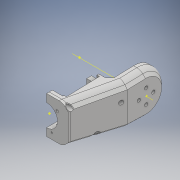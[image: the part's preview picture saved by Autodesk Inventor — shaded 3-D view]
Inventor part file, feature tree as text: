
AUTODESK INVENTOR PART (.ipt)
format: ipt  version: 2018 (Build 220112000, 112)  size: 1,074,688 bytes
history: native  units: mm
features: projected_geometry x48, sketch x45, extrude x37, hole x13, fillet x11, other x10, chamfer x9, reference x3, mirror x1, plane x1
ambient origin geometry x8: Origin, YZ Plane, XZ Plane, XY Plane, X Axis, Y Axis, Z Axis, Center Point
bodies: Solid1 (feature_tree)
feature tree (178):
  extrude  "Extrusion1"  Depth=45.0mm
  extrude  "Extrusion2"  Depth=2.25mm
  hole  "Hole1"  [1 undecoded]
  hole  "Hole2"  [1 undecoded]
  fillet  "Fillet1"  Radius=14.0mm
  extrude  "Extrusion3"  Depth=18.5mm
  extrude  "Extrusion4"  Depth=10.0mm
  extrude  "Extrusion5"  Depth=2.0mm
  extrude  "Extrusion6"  Depth=2.0mm
  hole  "Hole3"  [1 undecoded]
  extrude  "Extrusion7"  Depth=2.0mm
  extrude  "Extrusion8"  Depth=1.0mm TaperAngle=0.0deg
  extrude  "Extrusion9"  Depth=24.5mm
  extrude  "Extrusion10"  Depth=10.0mm
  extrude  "Extrusion11"  Depth=14.5mm
  extrude  "Extrusion13"  Depth=14.5mm
  extrude  "Extrusion14"  Depth=5.0mm
  extrude  "Extrusion15"  Depth=2.25mm
  extrude  "Extrusion16"  Depth=5.0mm
  extrude  "Extrusion17"  Depth=9.0mm
  chamfer  "Chamfer1"  Distance=1.0mm
  fillet  "Fillet7"  Radius=20.7mm
  fillet  "Fillet8"  Radius=32.0mm
  mirror  "Mirror1"
  sketch  "Sketch26"  dims[d55=2.25mm d56=5.0mm]
  extrude  "Extrusion24"  Depth=1.0mm TaperAngle=0.0deg
  extrude  "Extrusion25"  Depth=8.0mm
  extrude  "Extrusion26"  Depth=0.2mm TaperAngle=0.0deg
  extrude  "Extrusion27"  Depth=5.0mm TaperAngle=0.0deg
  other  "Work Axis1"
  plane  "Work Plane2"
  extrude  "Extrusion28"  Depth=0.2mm TaperAngle=0.0deg
  extrude  "Extrusion29"  Depth=2.0mm TaperAngle=45.0deg
  chamfer  "Chamfer2"  Distance=15.0mm
  extrude  "Extrusion31"  Depth=15.0mm TaperAngle=0.0deg
  chamfer  "Chamfer3"  Distance=15.0mm
  chamfer  "Chamfer4"  Distance=100.0mm
  extrude  "Extrusion32"  Depth=2.0mm TaperAngle=45.0deg
  chamfer  "Chamfer5"  [1 undecoded]
  extrude  "Extrusion33"  Depth=2.0mm
  sketch  "Sketch41"  dims[d100=0.2mm d101=0.0mm d102=2.5mm d103=2.0mm d104=45.0deg]
  extrude  "Extrusion34"  Depth=2.0mm
  chamfer  "Chamfer6"  Distance=11.5mm
  fillet  "Fillet9"  Radius=100.0mm
  extrude  "Extrusion35"  Depth=2.0mm TaperAngle=45.0deg
  extrude  "Extrusion36"  Depth=2.0mm TaperAngle=45.0deg
  chamfer  "Chamfer7"  Distance=7.0mm
  fillet  "Fillet10"  Radius=100.0mm
  extrude  "Extrusion37"  Depth=2.0mm TaperAngle=45.0deg
  extrude  "Extrusion38"  Depth=2.0mm TaperAngle=0.0deg
  extrude  "Extrusion39"  Depth=2.0mm TaperAngle=0.0deg
  extrude  "Extrusion40"  Depth=2.0mm TaperAngle=45.0deg
  chamfer  "Chamfer8"  Distance=8.0mm
  chamfer  "Chamfer9"  Angle=15.0deg  [1 undecoded]
  hole  "Hole6"  [1 undecoded]
  fillet  "Fillet11"  Radius=15.470628mm
  fillet  "Fillet12"  Radius=2.5mm
  extrude  "Extrusion41"  Depth=2.0mm TaperAngle=0.0deg
  extrude  "Extrusion42"  Depth=2.0mm TaperAngle=45.0deg
  hole  "Hole7"  [1 undecoded]
  extrude  "Extrusion43"  TaperAngle=15.0deg  [1 undecoded]
  extrude  "Extrusion44"  Depth=2.0mm
  sketch  "Sketch58"  dims[d162=5.0mm d165=100.0mm d166=0.0mm]
  hole  "Hole8"  [1 undecoded]
  hole  "Hole9"  [1 undecoded]
  hole  "Hole10"  [1 undecoded]
  hole  "Hole11"  [1 undecoded]
  hole  "Hole12"  [1 undecoded]
  hole  "Hole13"  [1 undecoded]
  hole  "Hole14"  [1 undecoded]
  hole  "Hole15"  [1 undecoded]
  extrude  "Extrusion45"  Depth=2.0mm
  fillet  "Fillet14"  Radius=0.75mm
  fillet  "Fillet15"  Radius=20.5mm
  fillet  "Fillet16"  Radius=3.05mm
  fillet  "Fillet17"  Radius=14.0mm
  sketch  "Sketch1"  dims[d0=24.5mm d1=45.0mm]
  sketch  "Sketch2"  dims[d2=1.95mm d3=0.0mm d4=2.25mm]
  projected_geometry  "Projected Loop1"
  sketch  "Sketch3"  dims[d5=20.0mm d6=2.25mm]
  projected_geometry  "Projected Loop2"
  sketch  "Sketch4"  dims[d7=5.25mm d8=5.25mm d9=14.0mm]
  projected_geometry  "Projected Loop3"
  sketch  "Sketch5"  dims[d10=5.25mm d11=18.5mm]
  projected_geometry  "Projected Loop4"
  sketch  "Sketch6"  dims[d12=10.0mm d13=0.0mm d14=20.5mm]
  projected_geometry  "Projected Loop5"
  sketch  "Sketch7"  dims[d15=2.0mm d16=2.195mm]
  projected_geometry  "Projected Loop6"
  sketch  "Sketch8"  dims[d17=2.0mm]
  projected_geometry  "Projected Loop7"
  sketch  "Sketch9"  dims[d18=2.4mm d19=6.0mm d20=4.4mm d21=2.0mm d22=90.0deg d23=8.0mm d24=20.594885mm d25=20.5mm]
  projected_geometry  "Projected Loop8"
  projected_geometry  "Projected Loop9"
  sketch  "Sketch10"  dims[d26=26.65mm d27=2.0mm]
  projected_geometry  "Projected Loop10"
  projected_geometry  "Projected Loop11"
  sketch  "Sketch11"  dims[d28=2.0mm]
  projected_geometry  "Projected Loop12"
  sketch  "Sketch12"  dims[d29=2.4mm d30=6.0mm d31=4.4mm d32=2.0mm d33=90.0deg d34=8.0mm d35=20.594885mm d36=0.5mm]
  sketch  "Sketch13"  dims[d37=18.0mm d38=1.0mm d39=0.0mm]
  sketch  "Sketch14"  dims[d41=5.0mm d42=0.0mm d43=24.5mm]
  projected_geometry  "Projected Loop13"
  sketch  "Sketch16"  dims[d44=1.15mm d45=0.0mm d46=10.0mm]
  projected_geometry  "Projected Loop14"
  sketch  "Sketch17"  dims[d47=21.0mm d48=14.5mm]
  projected_geometry  "Projected Loop15"
  sketch  "Sketch18"  dims[d49=20.0mm d50=14.5mm]
  projected_geometry  "Projected Loop16"
  sketch  "Sketch19"  dims[d51=24.5mm d52=5.0mm]
  projected_geometry  "Projected Loop17"
  sketch  "Sketch20"  dims[d53=5.0mm d54=2.25mm]
  projected_geometry  "Projected Loop18"
  projected_geometry  "Projected Loop25"
  sketch  "Sketch31"  dims[d57=5.0mm d58=9.0mm]
  projected_geometry  "Projected Loop30"
  reference  "Reference1"
  sketch  "Sketch32"  dims[d59=14.75mm]
  projected_geometry  "Projected Loop31"
  sketch  "Sketch33"  dims[d60=4.0mm d61=1.0mm d62=0.0mm d63=20.7mm]
  projected_geometry  "Projected Loop32"
  sketch  "Sketch34"  dims[d64=2.4mm d65=6.0mm d66=4.4mm d67=2.0mm d68=90.0deg d69=8.0mm d70=20.594885mm d72=32.0mm]
  projected_geometry  "Projected Loop33"
  other  "Work Point1"
  other  "Work Point2"
  other  "Work Point3"
  sketch  "Sketch35"  dims[d73=3.0mm d74=0.0mm d75=1.0mm d76=0.0mm]
  sketch  "Sketch37"  dims[d77=12.25mm d78=0.0mm d80=8.0mm]
  projected_geometry  "Projected Loop34"
  sketch  "Sketch38"  dims[d81=4.5mm d82=0.0mm d84=0.2mm d85=0.0mm]
  sketch  "Sketch39"  dims[d91=8.0mm d92=0.0mm d93=5.0mm d94=0.0mm]
  sketch  "Sketch40"  dims[d95=5.0mm d96=0.0mm d98=0.2mm d99=0.0mm]
  projected_geometry  "Projected Loop35"
  projected_geometry  "Projected Loop36"
  projected_geometry  "Projected Loop37"
  projected_geometry  "Projected Loop38"
  sketch  "Sketch42"  dims[d105=1.5mm]
  projected_geometry  "Projected Loop39"
  sketch  "Sketch43"  dims[d114=0.5mm]
  reference  "Reference2"
  reference  "Reference3"
  sketch  "Sketch45"  dims[d130=60.0mm]
  projected_geometry  "Projected Loop40"
  sketch  "Sketch46"  dims[d131=36.0mm]
  projected_geometry  "Projected Loop41"
  sketch  "Sketch48"  dims[d146=40.0mm]
  projected_geometry  "Projected Loop43"
  sketch  "Sketch49"  dims[d147=60.0mm]
  projected_geometry  "Projected Loop44"
  projected_geometry  "Projected Loop45"
  sketch  "Sketch50"  dims[d148=0.0mm]
  projected_geometry  "Projected Loop46"
  sketch  "Sketch52"  dims[d149=2.3mm d150=15.0mm d151=0.0mm]
  sketch  "Sketch53"  dims[d152=15.0mm d153=0.0mm d154=15.0mm d155=0.0mm d156=15.0mm d157=0.0mm]
  projected_geometry  "Projected Loop47"
  sketch  "Sketch54"  dims[d158=20.5mm]
  projected_geometry  "Projected Loop48"
  sketch  "Sketch55"  dims[d159=41.5mm]
  sketch  "Sketch56"  dims[d160=15.5mm]
  projected_geometry  "Projected Loop49"
  sketch  "Sketch57"  dims[d161=15.5mm]
  projected_geometry  "Projected Loop50"
  projected_geometry  "Projected Loop51"
  projected_geometry  "Projected Loop52"
  projected_geometry  "Projected Loop53"
  projected_geometry  "Projected Loop54"
  projected_geometry  "Projected Loop55"
  projected_geometry  "Projected Loop56"
  projected_geometry  "Projected Loop57"
  sketch  "Sketch59"  dims[d167=100.0mm d168=0.0mm d169=6.0mm d170=2.0mm d171=45.0deg d172=0.0mm d173=11.5mm d175=11.5mm d176=11.5mm d179=100.0mm d180=0.0mm d181=5.0mm d182=2.0mm d183=45.0deg d184=5.0mm d185=2.0mm d186=45.0deg d187=7.0mm d188=100.0mm d189=0.0mm d190=5.0mm d191=2.0mm d192=45.0deg d193=100.0mm d194=0.0mm d195=100.0mm d196=0.0mm d197=5.0mm d198=2.0mm d199=45.0deg d200=8.0mm d202=15.0deg d204=10.970628mm d205=15.470628mm d206=2.5mm d207=0.0mm d208=2.5mm d209=0.0mm d210=3.0mm d211=2.0mm d212=45.0deg d213=2.0mm d215=15.0deg d216=4.0mm d217=4.0mm d218=5.0mm d219=0.0mm d222=32.0mm d223=4.0mm d224=0.0mm d225=2.5mm d226=0.0mm d227=6.5mm d228=0.0mm d229=3.0mm d230=2.0mm d231=45.0deg d232=3.0mm d233=2.0mm d234=45.0deg d235=1.567mm d236=15.0mm d237=4.0mm d238=2.0mm d239=90.0deg d240=15.0mm d241=20.594885mm d242=2.0mm d243=0.75mm d244=20.5mm d245=3.05mm d246=0.0mm d247=14.0mm d248=3.2mm d249=6.0mm d250=4.0mm d251=2.0mm d252=90.0deg d253=8.8mm d254=20.594885mm d255=20.5mm d256=1.55mm d257=0.0mm d258=8.0mm d259=2.5mm d260=0.0mm d261=8.0mm d262=2.5mm d263=0.0mm d266=4.624622mm d267=4.624622mm d268=2.75mm d269=2.75mm d270=2.35mm d271=2.35mm d272=14.0mm d273=4.0mm d274=5.6mm d275=3.708mm d276=3.023mm d277=2.0mm d278=14.3117mm d279=17.0mm d280=0.0mm d281=4.0mm d282=3.708mm d283=3.023mm d284=2.0mm d285=14.3117mm d286=19.0mm d287=0.0mm d288=4.0mm d289=3.708mm d290=3.023mm d291=2.0mm d292=14.3117mm d293=13.0mm d294=0.0mm d295=2.3mm d296=4.0mm d297=4.4mm d298=2.0mm d299=90.0deg d300=32.25mm d301=0.0mm d302=3.3mm d303=4.0mm d304=6.3mm d305=2.0mm d306=90.0deg d307=32.25mm d308=0.0mm d309=1.567mm d310=4.0mm d311=6.3mm d312=2.0mm d313=90.0deg d314=45.0mm d315=20.594885mm d316=1.567mm d317=4.0mm d318=6.3mm d319=2.0mm d320=90.0deg d321=55.0mm d322=20.594885mm d323=2.459mm d324=6.0mm d325=6.3mm d326=2.0mm d327=90.0deg d328=50.0mm d329=20.594885mm d330=32.25mm d331=0.0mm d333=0.5mm d334=0.4mm d335=1.0mm d336=2.0mm]
  parser-record x1  (decoder bookkeeping rows leaked as tree rows — omitted from the tree; the rows remain in map.json)
  other  "servocheck.iam"
  other  "LX-16A:3"
  other  "DUOPAN-SG-SJ_10"
  projected_geometry  "Project Cut Edges1"
  projected_geometry  "Project Cut Edges3"
  other  "bottomarm:1"
  other  "arm1:1"
note: 16 required parameter values undecoded (feature->parameter linkage not recoverable at this tier; creation-order binding heuristic only, values carry confidence <= 0.55)
note: 1 file-system path scrubbed to <path> (originals preserved in map.json)
